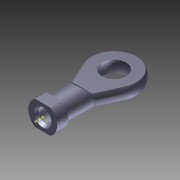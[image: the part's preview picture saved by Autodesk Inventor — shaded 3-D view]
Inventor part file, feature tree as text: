
AUTODESK INVENTOR PART (.ipt)
format: ipt  version: 2011 (Build 150239000, 239)  size: 185,856 bytes
history: native  units: mm
features: other x4, plane x2, imported_body x1, sketch x1
ambient origin geometry x8: Origin, YZ Plane, XZ Plane, XY Plane, X Axis, Y Axis, Z Axis, Center Point
bodies: Solid1 (feature_tree)
feature tree (8):
  imported_body  "Base1"
  sketch  "Sketch1"  dims[d0=3.175mm d1=6.35mm]
  other  "Work Point2"
  other  "Work Point3"
  plane  "Work Plane1"
  other  "Work Axis1"
  plane  "Work Plane2"
  other  "Work Axis2"
